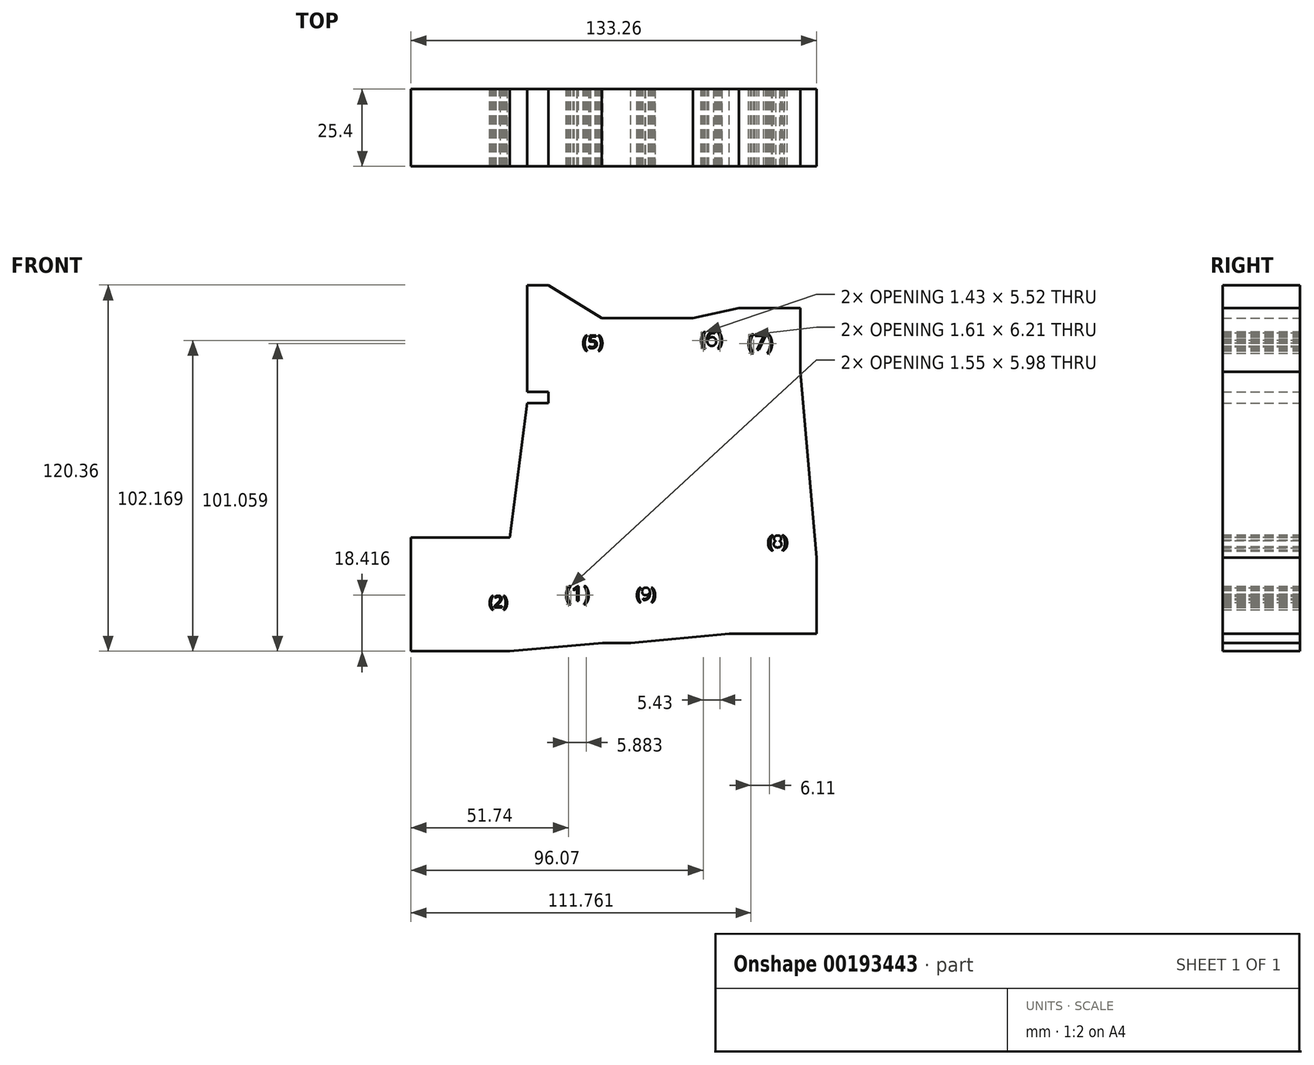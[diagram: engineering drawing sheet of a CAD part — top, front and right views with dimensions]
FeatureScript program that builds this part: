
annotation { "Feature Type Name" : "Feature", "Feature Type Description" : "" }
export const myFeature = defineFeature(function(context is Context, id is Id, definition is map)
    precondition{}
    {
        {
            var Q0;
            Q0=qCreatedBy(makeId("Front.planeOp"),FACE);
            var sketch = newSketch(context, id + "F0", { "sketchPlane" : qUnion([Q0])});
            skLineSegment(sketch, "E0.bottom", {"start": v(-72.52, 74.7) * mm, "end": v(-23.16, 74.7) * mm});
            skLineSegment(sketch, "E0.top", {"start": v(-72.52, 35.97) * mm, "end": v(-23.16, 35.97) * mm});
            skLineSegment(sketch, "E0.left", {"start": v(-72.52, 74.7) * mm, "end": v(-72.52, 35.97) * mm});
            skLineSegment(sketch, "E0.right", {"start": v(-23.16, 74.7) * mm, "end": v(-23.16, 35.97) * mm});
            skLineSegment(sketch, "E1.bottom", {"start": v(-30.16, 74.7) * mm, "end": v(-23.16, 74.7) * mm});
            skLineSegment(sketch, "E1.top", {"start": v(-30.16, 35.97) * mm, "end": v(-23.16, 35.97) * mm});
            skLineSegment(sketch, "E1.right", {"start": v(-30.16, 74.7) * mm, "end": v(-30.16, 35.97) * mm});
            skLineSegment(sketch, "E2.bottom", {"start": v(24.3, 63.88) * mm, "end": v(-5.7, 63.88) * mm});
            skLineSegment(sketch, "E2.top", {"start": v(24.3, 49.64) * mm, "end": v(-5.7, 49.64) * mm});
            skLineSegment(sketch, "E2.left", {"start": v(24.3, 63.88) * mm, "end": v(24.3, 49.64) * mm});
            skLineSegment(sketch, "E2.right", {"start": v(-5.7, 63.88) * mm, "end": v(-5.7, 49.64) * mm});
            skLineSegment(sketch, "E3.bottom", {"start": v(59.6, 67.1) * mm, "end": v(39.48, 67.1) * mm});
            skLineSegment(sketch, "E3.top", {"start": v(59.6, 46.22) * mm, "end": v(39.48, 46.22) * mm});
            skLineSegment(sketch, "E3.left", {"start": v(59.6, 67.1) * mm, "end": v(59.6, 46.22) * mm});
            skLineSegment(sketch, "E3.right", {"start": v(39.48, 67.1) * mm, "end": v(39.48, 46.22) * mm});
            skLineSegment(sketch, "E4.bottom", {"start": v(64.92, -13.23) * mm, "end": v(36.26, -13.23) * mm});
            skLineSegment(sketch, "E4.top", {"start": v(64.92, -39.96) * mm, "end": v(36.26, -39.96) * mm});
            skLineSegment(sketch, "E4.left", {"start": v(64.92, -13.23) * mm, "end": v(64.92, -39.96) * mm});
            skLineSegment(sketch, "E4.right", {"start": v(36.26, -13.23) * mm, "end": v(36.26, -39.96) * mm});
            skLineSegment(sketch, "E5.bottom", {"start": v(3.88, -10.85) * mm, "end": v(-5.44, -10.85) * mm});
            skLineSegment(sketch, "E5.top", {"start": v(3.88, -42.92) * mm, "end": v(-5.44, -42.92) * mm});
            skLineSegment(sketch, "E5.left", {"start": v(3.88, -10.85) * mm, "end": v(3.88, -42.92) * mm});
            skLineSegment(sketch, "E5.right", {"start": v(-5.44, -10.85) * mm, "end": v(-5.44, -42.92) * mm});
            skLineSegment(sketch, "E6.bottom", {"start": v(-35.82, -8.26) * mm, "end": v(-68.34, -8.26) * mm});
            skLineSegment(sketch, "E6.top", {"start": v(-35.82, -45.65) * mm, "end": v(-68.34, -45.65) * mm});
            skLineSegment(sketch, "E6.left", {"start": v(-35.82, -8.26) * mm, "end": v(-35.82, -45.65) * mm});
            skLineSegment(sketch, "E6.right", {"start": v(-68.34, -8.26) * mm, "end": v(-68.34, -45.65) * mm});
            skLineSegment(sketch, "E7", {"start": v(-23.16, 74.7) * mm, "end": v(-5.7, 63.88) * mm});
            skLineSegment(sketch, "E8", {"start": v(-5.7, 49.64) * mm, "end": v(-23.16, 35.97) * mm});
            skLineSegment(sketch, "E9", {"start": v(24.3, 63.88) * mm, "end": v(39.48, 67.1) * mm});
            skLineSegment(sketch, "E10", {"start": v(24.3, 49.64) * mm, "end": v(39.48, 46.22) * mm});
            skLineSegment(sketch, "E11", {"start": v(36.26, -13.23) * mm, "end": v(3.88, -10.85) * mm});
            skLineSegment(sketch, "E12", {"start": v(36.26, -39.96) * mm, "end": v(3.88, -42.92) * mm});
            skLineSegment(sketch, "E13", {"start": v(-5.44, -10.85) * mm, "end": v(-35.82, -8.26) * mm});
            skLineSegment(sketch, "E14", {"start": v(-5.44, -42.92) * mm, "end": v(-35.88, -45.65) * mm});
            skLineSegment(sketch, "E15", {"start": v(39.48, 46.22) * mm, "end": v(36.26, -13.23) * mm});
            skLineSegment(sketch, "E16", {"start": v(59.6, 46.22) * mm, "end": v(64.92, -14.9) * mm});
            skLineSegment(sketch, "E17", {"start": v(-30.16, 35.97) * mm, "end": v(-35.82, -8.26) * mm});
            skLineSegment(sketch, "E18", {"start": v(-72.52, 35.97) * mm, "end": v(-68.34, -8.26) * mm});
            skLineSegment(sketch, "E19", {"start": v(-30.16, 72.04) * mm, "end": v(-23.16, 72.04) * mm});
            skLineSegment(sketch, "E20", {"start": v(-30.16, 68.81) * mm, "end": v(-23.16, 68.81) * mm});
            skLineSegment(sketch, "E21", {"start": v(-30.16, 65.4) * mm, "end": v(-23.16, 65.4) * mm});
            skLineSegment(sketch, "E22", {"start": v(-30.16, 62.17) * mm, "end": v(-23.16, 62.17) * mm});
            skLineSegment(sketch, "E23", {"start": v(-30.16, 58.75) * mm, "end": v(-23.16, 58.75) * mm});
            skLineSegment(sketch, "E24", {"start": v(-30.16, 55.34) * mm, "end": v(-23.16, 55.34) * mm});
            skLineSegment(sketch, "E25", {"start": v(-30.16, 52.3) * mm, "end": v(-23.16, 52.3) * mm});
            skLineSegment(sketch, "E26", {"start": v(-30.16, 48.88) * mm, "end": v(-23.16, 48.88) * mm});
            skLineSegment(sketch, "E27", {"start": v(-30.16, 45.46) * mm, "end": v(-23.16, 45.46) * mm});
            skLineSegment(sketch, "E28", {"start": v(-30.16, 42.43) * mm, "end": v(-23.16, 42.43) * mm});
            skLineSegment(sketch, "E29", {"start": v(-30.16, 39.58) * mm, "end": v(-23.16, 39.58) * mm});
            skText(sketch, "E30", { "text": "(8)", "fontName": "Tinos-Bold.ttf"});
            skPoint(sketch, "E31", {"position": v(50.59, -13.23) * mm});
            skPoint(sketch, "E32", {"position": v(3.88, -26.89) * mm});
            skPoint(sketch, "E33", {"position": v(-5.44, -26.89) * mm});
            skPoint(sketch, "E34", {"position": v(-35.82, -30.28) * mm});
            skPoint(sketch, "E35", {"position": v(-52.77, 35.97) * mm});
            skPoint(sketch, "E36", {"position": v(-26.66, 55.34) * mm});
            skPoint(sketch, "E37", {"position": v(-5.7, 56.76) * mm});
            skPoint(sketch, "E38", {"position": v(24.3, 56.76) * mm});
            skPoint(sketch, "E39", {"position": v(39.48, 56.66) * mm});
            skText(sketch, "E40", { "text": "(9)", "fontName": "OpenSans-Regular.ttf"});
            skText(sketch, "E41", { "text": "(1)\n", "fontName": "OpenSans-Regular.ttf"});
            skText(sketch, "E42", { "text": "(2)\n", "fontName": "OpenSans-Regular.ttf"});
            skText(sketch, "E43", { "text": "(3)", "fontName": "OpenSans-Regular.ttf"});
            skText(sketch, "E44", { "text": "(4)\n", "fontName": "OpenSans-Regular.ttf"});
            skText(sketch, "E45", { "text": "(5)", "fontName": "OpenSans-Regular.ttf"});
            skText(sketch, "E46", { "text": "(6)", "fontName": "OpenSans-Regular.ttf"});
            skText(sketch, "E47", { "text": "(7)", "fontName": "OpenSans-Regular.ttf"});
            const initialGuessF0  = {"E30": [0.04878, -0.01148, 1, 0, 0.00418], "E40": [0.0057, -0.02876, 1, 0, 0.00399], "E41": [-0.01765, -0.02914, 1, 0, 0.00494], "E42": [-0.0427, -0.03123, 1, 0, 0.0038], "E43": [-0.05486, 0.02819, 1, 0, 0.00418], "E44": [-0.04005, 0.05154, 1, 0, 0.00522], "E45": [-0.01196, 0.054, 1, 0, 0.00418], "E46": [0.02676, 0.05476, 1, 0, 0.00456], "E47": [0.04233, 0.05343, 1, 0, 0.00513]};
            skSetInitialGuess(sketch, initialGuessF0);
            skSolve(sketch);
        }
        {
            var Q0;
            Q0=makeQuery(id+"F0.imprint","IMPRINT",FACE,{"disambiguationData":[TD([[makeQuery(id+"F0.imprint","IMPRINT",EDGE,{"derivedFrom":sQuery(id+"F0.wireOp",EDGE,"E0.top")}),-1.0]])]});
            var Q1;
            {var subQ7=sQuery(id+"F0.wireOp",EDGE,"E0.bottom");Q1=makeQuery(id+"F0.imprint","IMPRINT",FACE,{"disambiguationData":[TD([[makeQuery(id+"F0.imprint","IMPRINT",EDGE,{"derivedFrom":subQ7}),-1.0]])]});}
            var Q2;
            {var subQ0=sQuery(id+"F0.wireOp",EDGE,"E1.top");Q2=makeQuery(id+"F0.imprint","IMPRINT",FACE,{"disambiguationData":[TD([[makeQuery(id+"F0.imprint","IMPRINT",EDGE,{"derivedFrom":subQ0}),1.0]])]});}
            var Q3;
            {var subQ0=sQuery(id+"F0.wireOp",EDGE,"E28");Q3=makeQuery(id+"F0.imprint","IMPRINT",FACE,{"disambiguationData":[TD([[makeQuery(id+"F0.imprint","IMPRINT",EDGE,{"derivedFrom":subQ0}),-1.0]])]});}
            var Q4;
            {var subQ0=sQuery(id+"F0.wireOp",EDGE,"E27");Q4=makeQuery(id+"F0.imprint","IMPRINT",FACE,{"disambiguationData":[TD([[makeQuery(id+"F0.imprint","IMPRINT",EDGE,{"derivedFrom":subQ0}),-1.0]])]});}
            var Q5;
            {var subQ0=sQuery(id+"F0.wireOp",EDGE,"E26");Q5=makeQuery(id+"F0.imprint","IMPRINT",FACE,{"disambiguationData":[TD([[makeQuery(id+"F0.imprint","IMPRINT",EDGE,{"derivedFrom":subQ0}),-1.0]])]});}
            var Q6;
            {var subQ0=sQuery(id+"F0.wireOp",EDGE,"E25");Q6=makeQuery(id+"F0.imprint","IMPRINT",FACE,{"disambiguationData":[TD([[makeQuery(id+"F0.imprint","IMPRINT",EDGE,{"derivedFrom":subQ0}),-1.0]])]});}
            var Q7;
            {var subQ0=sQuery(id+"F0.wireOp",EDGE,"E24");Q7=makeQuery(id+"F0.imprint","IMPRINT",FACE,{"disambiguationData":[TD([[makeQuery(id+"F0.imprint","IMPRINT",EDGE,{"derivedFrom":subQ0}),-1.0]])]});}
            var Q8;
            {var subQ0=sQuery(id+"F0.wireOp",EDGE,"E23");Q8=makeQuery(id+"F0.imprint","IMPRINT",FACE,{"disambiguationData":[TD([[makeQuery(id+"F0.imprint","IMPRINT",EDGE,{"derivedFrom":subQ0}),-1.0]])]});}
            var Q9;
            {var subQ0=sQuery(id+"F0.wireOp",EDGE,"E22");Q9=makeQuery(id+"F0.imprint","IMPRINT",FACE,{"disambiguationData":[TD([[makeQuery(id+"F0.imprint","IMPRINT",EDGE,{"derivedFrom":subQ0}),-1.0]])]});}
            var Q10;
            {var subQ0=sQuery(id+"F0.wireOp",EDGE,"E21");Q10=makeQuery(id+"F0.imprint","IMPRINT",FACE,{"disambiguationData":[TD([[makeQuery(id+"F0.imprint","IMPRINT",EDGE,{"derivedFrom":subQ0}),-1.0]])]});}
            var Q11;
            {var subQ0=sQuery(id+"F0.wireOp",EDGE,"E20");Q11=makeQuery(id+"F0.imprint","IMPRINT",FACE,{"disambiguationData":[TD([[makeQuery(id+"F0.imprint","IMPRINT",EDGE,{"derivedFrom":subQ0}),-1.0]])]});}
            var Q12;
            {var subQ0=sQuery(id+"F0.wireOp",EDGE,"E19");Q12=makeQuery(id+"F0.imprint","IMPRINT",FACE,{"disambiguationData":[TD([[makeQuery(id+"F0.imprint","IMPRINT",EDGE,{"derivedFrom":subQ0}),-1.0]])]});}
            var Q13;
            {var subQ0=sQuery(id+"F0.wireOp",EDGE,"E1.bottom");Q13=makeQuery(id+"F0.imprint","IMPRINT",FACE,{"disambiguationData":[TD([[makeQuery(id+"F0.imprint","IMPRINT",EDGE,{"derivedFrom":subQ0}),-1.0]])]});}
            var Q14;
            Q14=makeQuery(id+"F0.imprint","IMPRINT",FACE,{"disambiguationData":[TD([[makeQuery(id+"F0.imprint","IMPRINT",EDGE,{"derivedFrom":sQuery(id+"F0.wireOp",EDGE,"E2.right")}),-1.0]])]});
            var Q15;
            Q15=makeQuery(id+"F0.imprint","IMPRINT",FACE,{"disambiguationData":[TD([[makeQuery(id+"F0.imprint","IMPRINT",EDGE,{"derivedFrom":sQuery(id+"F0.wireOp",EDGE,"E2.bottom")}),1.0]])]});
            var Q16;
            Q16=makeQuery(id+"F0.imprint","IMPRINT",FACE,{"disambiguationData":[TD([[makeQuery(id+"F0.imprint","IMPRINT",EDGE,{"derivedFrom":sQuery(id+"F0.wireOp",EDGE,"E2.left")}),1.0]])]});
            var Q17;
            Q17=makeQuery(id+"F0.imprint","IMPRINT",FACE,{"disambiguationData":[TD([[makeQuery(id+"F0.imprint","IMPRINT",EDGE,{"derivedFrom":sQuery(id+"F0.wireOp",EDGE,"E3.bottom")}),1.0]])]});
            var Q18;
            {var subQ0=sQuery(id+"F0.wireOp",EDGE,"E3.top");Q18=makeQuery(id+"F0.imprint","IMPRINT",FACE,{"disambiguationData":[TD([[makeQuery(id+"F0.imprint","IMPRINT",EDGE,{"derivedFrom":subQ0}),1.0]])]});}
            var Q19;
            {var subQ2=sQuery(id+"F0.wireOp",EDGE,"E4.top");Q19=makeQuery(id+"F0.imprint","IMPRINT",FACE,{"disambiguationData":[TD([[makeQuery(id+"F0.imprint","IMPRINT",EDGE,{"derivedFrom":subQ2}),-1.0]])]});}
            var Q20;
            Q20=makeQuery(id+"F0.imprint","IMPRINT",FACE,{"disambiguationData":[TD([[makeQuery(id+"F0.imprint","IMPRINT",EDGE,{"derivedFrom":sQuery(id+"F0.wireOp",EDGE,"E4.right")}),-1.0]])]});
            var Q21;
            Q21=makeQuery(id+"F0.imprint","IMPRINT",FACE,{"disambiguationData":[TD([[makeQuery(id+"F0.imprint","IMPRINT",EDGE,{"derivedFrom":sQuery(id+"F0.wireOp",EDGE,"E5.bottom")}),1.0]])]});
            var Q22;
            {var subQ0=sQuery(id+"F0.wireOp",EDGE,"E5.right");Q22=makeQuery(id+"F0.imprint","IMPRINT",FACE,{"disambiguationData":[TD([[makeQuery(id+"F0.imprint","IMPRINT",EDGE,{"derivedFrom":subQ0}),-1.0]])]});}
            var Q23;
            {var subQ2=sQuery(id+"F0.wireOp",EDGE,"E6.bottom");Q23=makeQuery(id+"F0.imprint","IMPRINT",FACE,{"disambiguationData":[TD([[makeQuery(id+"F0.imprint","IMPRINT",EDGE,{"derivedFrom":subQ2}),1.0]])]});}
            extrude(context, id + "F1", {"entities" : qUnion([Q0, Q1, Q2, Q3, Q4, Q5, Q6, Q7, Q8, Q9, Q10, Q11, Q12, Q13, Q14, Q15, Q16, Q17, Q18, Q19, Q20, Q21, Q22, Q23]), "endBound" : BoundingType.SYMMETRIC, "depth" : 25.4 * mm});
        }
    });
